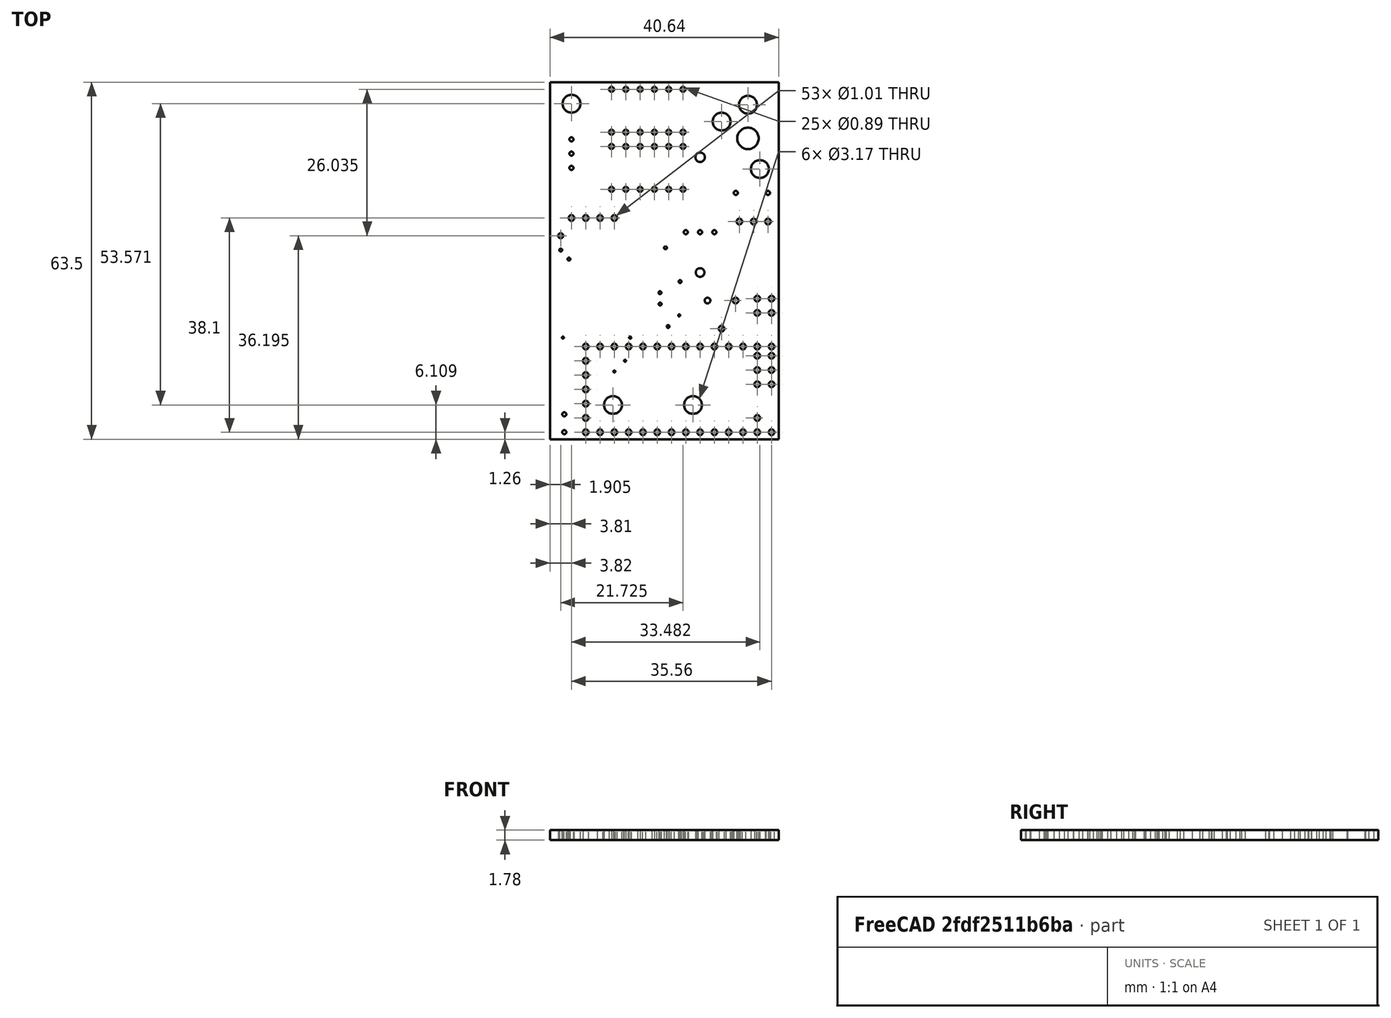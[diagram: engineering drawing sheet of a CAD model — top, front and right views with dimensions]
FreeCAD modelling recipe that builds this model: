
FCSTD DOCUMENT  (FreeCAD 1.0R39109 (Git))
Label: PCB-generated
License: All rights reserved
LicenseURL: https://en.wikipedia.org/wiki/All_rights_reserved
objects: Sketcher::SketchObject×2, PartDesign::Pad×1, PartDesign::Pocket×1, PartDesign::Body×1
note: 11 computed .brp shape members not serialized (recipe doc carries the construction recipe); baked Part::Feature solids carry a one-line shape summary decoded from their .brp

FEATURE [Sketcher::SketchObject] HoleSketch
  ArcFitTolerance = 1e-06
  AttachmentSupport = -> [XY_Plane]
  FullyConstrained = false
  MakeInternals = false
  MapMode = 5
  sketch-geometry (110):
    g0: Circle CenterX=35.1848 CenterY=59.5072 CenterZ=0 NormalX=0 NormalY=0 NormalZ=1 AngleXU=0 Radius=1.5875
    g1: Circle CenterX=35.1752 CenterY=53.5132 CenterZ=0 NormalX=0 NormalY=0 NormalZ=1 AngleXU=0 Radius=1.905
    g2: Circle CenterX=30.4896 CenterY=56.5054 CenterZ=0 NormalX=0 NormalY=0 NormalZ=1 AngleXU=0 Radius=1.5875
    g3: Circle CenterX=3.36742 CenterY=32.0386 CenterZ=0 NormalX=0 NormalY=0 NormalZ=1 AngleXU=0 Radius=0.250152
    g4: Circle CenterX=20.9935 CenterY=20.0698 CenterZ=0 NormalX=0 NormalY=0 NormalZ=1 AngleXU=0 Radius=0.250152
    g5: Circle CenterX=1.905 CenterY=33.6646 CenterZ=0 NormalX=0 NormalY=0 NormalZ=1 AngleXU=0 Radius=0.254962
    g6: Circle CenterX=20.522 CenterY=34.0591 CenterZ=0 NormalX=0 NormalY=0 NormalZ=1 AngleXU=0 Radius=0.254962
    g7: Circle CenterX=19.5407 CenterY=26.0735 CenterZ=0 NormalX=0 NormalY=0 NormalZ=1 AngleXU=0 Radius=0.254962
    g8: Circle CenterX=19.5695 CenterY=24.0627 CenterZ=0 NormalX=0 NormalY=0 NormalZ=1 AngleXU=0 Radius=0.254962
    g9: Circle CenterX=23.6297 CenterY=62.23 CenterZ=0 NormalX=0 NormalY=0 NormalZ=1 AngleXU=0 Radius=0.442576
    g10: Circle CenterX=23.6297 CenterY=54.61 CenterZ=0 NormalX=0 NormalY=0 NormalZ=1 AngleXU=0 Radius=0.442576
    g11: Circle CenterX=21.0897 CenterY=62.23 CenterZ=0 NormalX=0 NormalY=0 NormalZ=1 AngleXU=0 Radius=0.442576
    g12: Circle CenterX=21.0897 CenterY=54.61 CenterZ=0 NormalX=0 NormalY=0 NormalZ=1 AngleXU=0 Radius=0.442576
    g13: Circle CenterX=18.5497 CenterY=62.23 CenterZ=0 NormalX=0 NormalY=0 NormalZ=1 AngleXU=0 Radius=0.442576
    g14: Circle CenterX=18.5497 CenterY=54.61 CenterZ=0 NormalX=0 NormalY=0 NormalZ=1 AngleXU=0 Radius=0.442576
    g15: Circle CenterX=16.0097 CenterY=62.23 CenterZ=0 NormalX=0 NormalY=0 NormalZ=1 AngleXU=0 Radius=0.442576
    g16: Circle CenterX=16.0097 CenterY=54.61 CenterZ=0 NormalX=0 NormalY=0 NormalZ=1 AngleXU=0 Radius=0.442576
    g17: Circle CenterX=13.4697 CenterY=62.23 CenterZ=0 NormalX=0 NormalY=0 NormalZ=1 AngleXU=0 Radius=0.442576
    g18: Circle CenterX=10.9297 CenterY=62.23 CenterZ=0 NormalX=0 NormalY=0 NormalZ=1 AngleXU=0 Radius=0.442576
    g19: Circle CenterX=13.4697 CenterY=54.61 CenterZ=0 NormalX=0 NormalY=0 NormalZ=1 AngleXU=0 Radius=0.442576
    g20: Circle CenterX=10.9297 CenterY=54.61 CenterZ=0 NormalX=0 NormalY=0 NormalZ=1 AngleXU=0 Radius=0.442576
    g21: Circle CenterX=6.35 CenterY=1.26038 CenterZ=0 NormalX=0 NormalY=0 NormalZ=1 AngleXU=0 Radius=0.505114
    g22: Circle CenterX=8.89 CenterY=1.26038 CenterZ=0 NormalX=0 NormalY=0 NormalZ=1 AngleXU=0 Radius=0.505114
    g23: Circle CenterX=11.43 CenterY=1.26038 CenterZ=0 NormalX=0 NormalY=0 NormalZ=1 AngleXU=0 Radius=0.505114
    g24: Circle CenterX=6.35 CenterY=16.5004 CenterZ=0 NormalX=0 NormalY=0 NormalZ=1 AngleXU=0 Radius=0.505114
    g25: Circle CenterX=6.35 CenterY=3.80038 CenterZ=0 NormalX=0 NormalY=0 NormalZ=1 AngleXU=0 Radius=0.505114
    g26: Circle CenterX=6.35 CenterY=6.34038 CenterZ=0 NormalX=0 NormalY=0 NormalZ=1 AngleXU=0 Radius=0.505114
    g27: Circle CenterX=6.35 CenterY=8.88038 CenterZ=0 NormalX=0 NormalY=0 NormalZ=1 AngleXU=0 Radius=0.505114
    g28: Circle CenterX=6.35 CenterY=11.4204 CenterZ=0 NormalX=0 NormalY=0 NormalZ=1 AngleXU=0 Radius=0.505114
    g29: Circle CenterX=6.35 CenterY=13.9604 CenterZ=0 NormalX=0 NormalY=0 NormalZ=1 AngleXU=0 Radius=0.505114
    g30: Circle CenterX=13.97 CenterY=1.26038 CenterZ=0 NormalX=0 NormalY=0 NormalZ=1 AngleXU=0 Radius=0.505114
    g31: Circle CenterX=16.51 CenterY=1.26038 CenterZ=0 NormalX=0 NormalY=0 NormalZ=1 AngleXU=0 Radius=0.505114
    g32: Circle CenterX=19.05 CenterY=1.26038 CenterZ=0 NormalX=0 NormalY=0 NormalZ=1 AngleXU=0 Radius=0.505114
    g33: Circle CenterX=21.59 CenterY=1.26038 CenterZ=0 NormalX=0 NormalY=0 NormalZ=1 AngleXU=0 Radius=0.505114
    g34: Circle CenterX=24.13 CenterY=1.26038 CenterZ=0 NormalX=0 NormalY=0 NormalZ=1 AngleXU=0 Radius=0.505114
    g35: Circle CenterX=26.67 CenterY=1.26038 CenterZ=0 NormalX=0 NormalY=0 NormalZ=1 AngleXU=0 Radius=0.505114
    g36: Circle CenterX=29.21 CenterY=1.26038 CenterZ=0 NormalX=0 NormalY=0 NormalZ=1 AngleXU=0 Radius=0.505114
    g37: Circle CenterX=31.75 CenterY=1.26038 CenterZ=0 NormalX=0 NormalY=0 NormalZ=1 AngleXU=0 Radius=0.505114
    g38: Circle CenterX=34.29 CenterY=1.26038 CenterZ=0 NormalX=0 NormalY=0 NormalZ=1 AngleXU=0 Radius=0.505114
    g39: Circle CenterX=36.83 CenterY=1.26038 CenterZ=0 NormalX=0 NormalY=0 NormalZ=1 AngleXU=0 Radius=0.505114
    g40: Circle CenterX=39.37 CenterY=1.26038 CenterZ=0 NormalX=0 NormalY=0 NormalZ=1 AngleXU=0 Radius=0.505114
    g41: Circle CenterX=8.89 CenterY=16.5004 CenterZ=0 NormalX=0 NormalY=0 NormalZ=1 AngleXU=0 Radius=0.505114
    g42: Circle CenterX=11.43 CenterY=16.5004 CenterZ=0 NormalX=0 NormalY=0 NormalZ=1 AngleXU=0 Radius=0.505114
    g43: Circle CenterX=13.97 CenterY=16.5004 CenterZ=0 NormalX=0 NormalY=0 NormalZ=1 AngleXU=0 Radius=0.505114
    g44: Circle CenterX=16.51 CenterY=16.5004 CenterZ=0 NormalX=0 NormalY=0 NormalZ=1 AngleXU=0 Radius=0.505114
    g45: Circle CenterX=19.05 CenterY=16.5004 CenterZ=0 NormalX=0 NormalY=0 NormalZ=1 AngleXU=0 Radius=0.505114
    g46: Circle CenterX=21.59 CenterY=16.5004 CenterZ=0 NormalX=0 NormalY=0 NormalZ=1 AngleXU=0 Radius=0.505114
    g47: Circle CenterX=24.13 CenterY=16.5004 CenterZ=0 NormalX=0 NormalY=0 NormalZ=1 AngleXU=0 Radius=0.505114
    g48: Circle CenterX=26.67 CenterY=16.5004 CenterZ=0 NormalX=0 NormalY=0 NormalZ=1 AngleXU=0 Radius=0.505114
    g49: Circle CenterX=29.21 CenterY=16.5004 CenterZ=0 NormalX=0 NormalY=0 NormalZ=1 AngleXU=0 Radius=0.505114
    g50: Circle CenterX=31.75 CenterY=16.5004 CenterZ=0 NormalX=0 NormalY=0 NormalZ=1 AngleXU=0 Radius=0.505114
    g51: Circle CenterX=34.29 CenterY=16.5004 CenterZ=0 NormalX=0 NormalY=0 NormalZ=1 AngleXU=0 Radius=0.505114
    g52: Circle CenterX=36.83 CenterY=16.5004 CenterZ=0 NormalX=0 NormalY=0 NormalZ=1 AngleXU=0 Radius=0.505114
    g53: Circle CenterX=39.37 CenterY=16.5004 CenterZ=0 NormalX=0 NormalY=0 NormalZ=1 AngleXU=0 Radius=0.505114
    g54: Circle CenterX=36.83 CenterY=3.80038 CenterZ=0 NormalX=0 NormalY=0 NormalZ=1 AngleXU=0 Radius=0.505114
    g55: Circle CenterX=25.4096 CenterY=6.10947 CenterZ=0 NormalX=0 NormalY=0 NormalZ=1 AngleXU=0 Radius=1.5875
    g56: Circle CenterX=3.81962 CenterY=59.6804 CenterZ=0 NormalX=0 NormalY=0 NormalZ=1 AngleXU=0 Radius=1.5875
    g57: Circle CenterX=11.1895 CenterY=6.10947 CenterZ=0 NormalX=0 NormalY=0 NormalZ=1 AngleXU=0 Radius=1.5875
    g58: Circle CenterX=26.67 CenterY=29.6622 CenterZ=0 NormalX=0 NormalY=0 NormalZ=1 AngleXU=0 Radius=0.774508
    g59: Circle CenterX=26.67 CenterY=50.165 CenterZ=0 NormalX=0 NormalY=0 NormalZ=1 AngleXU=0 Radius=0.846667
    g60: Circle CenterX=39.37 CenterY=12.3248 CenterZ=0 NormalX=0 NormalY=0 NormalZ=1 AngleXU=0 Radius=0.505114
    g61: Circle CenterX=39.37 CenterY=9.78477 CenterZ=0 NormalX=0 NormalY=0 NormalZ=1 AngleXU=0 Radius=0.505114
    g62: Circle CenterX=36.83 CenterY=9.78477 CenterZ=0 NormalX=0 NormalY=0 NormalZ=1 AngleXU=0 Radius=0.505114
    g63: Circle CenterX=39.37 CenterY=14.8648 CenterZ=0 NormalX=0 NormalY=0 NormalZ=1 AngleXU=0 Radius=0.505114
    g64: Circle CenterX=36.83 CenterY=12.3248 CenterZ=0 NormalX=0 NormalY=0 NormalZ=1 AngleXU=0 Radius=0.505114
    g65: Circle CenterX=36.83 CenterY=14.8648 CenterZ=0 NormalX=0 NormalY=0 NormalZ=1 AngleXU=0 Radius=0.505114
    g66: Circle CenterX=30.48 CenterY=19.6754 CenterZ=0 NormalX=0 NormalY=0 NormalZ=1 AngleXU=0 Radius=0.505114
    g67: Circle CenterX=32.9815 CenterY=24.6784 CenterZ=0 NormalX=0 NormalY=0 NormalZ=1 AngleXU=0 Radius=0.505114
    g68: Circle CenterX=27.9881 CenterY=24.6784 CenterZ=0 NormalX=0 NormalY=0 NormalZ=1 AngleXU=0 Radius=0.509924
    g69: Circle CenterX=39.37 CenterY=22.4848 CenterZ=0 NormalX=0 NormalY=0 NormalZ=1 AngleXU=0 Radius=0.505114
    g70: Circle CenterX=36.83 CenterY=22.4848 CenterZ=0 NormalX=0 NormalY=0 NormalZ=1 AngleXU=0 Radius=0.505114
    g71: Circle CenterX=39.37 CenterY=25.0248 CenterZ=0 NormalX=0 NormalY=0 NormalZ=1 AngleXU=0 Radius=0.505114
    g72: Circle CenterX=36.83 CenterY=25.0248 CenterZ=0 NormalX=0 NormalY=0 NormalZ=1 AngleXU=0 Radius=0.505114
    g73: Circle CenterX=38.735 CenterY=38.7254 CenterZ=0 NormalX=0 NormalY=0 NormalZ=1 AngleXU=0 Radius=0.505114
    g74: Circle CenterX=33.655 CenterY=38.7254 CenterZ=0 NormalX=0 NormalY=0 NormalZ=1 AngleXU=0 Radius=0.505114
    g75: Circle CenterX=36.195 CenterY=38.7254 CenterZ=0 NormalX=0 NormalY=0 NormalZ=1 AngleXU=0 Radius=0.505114
    g76: Circle CenterX=37.3014 CenterY=48.058 CenterZ=0 NormalX=0 NormalY=0 NormalZ=1 AngleXU=0 Radius=1.5875
    g77: Circle CenterX=3.81 CenterY=48.26 CenterZ=0 NormalX=0 NormalY=0 NormalZ=1 AngleXU=0 Radius=0.365606
    g78: Circle CenterX=3.81 CenterY=53.34 CenterZ=0 NormalX=0 NormalY=0 NormalZ=1 AngleXU=0 Radius=0.365606
    g79: Circle CenterX=3.81 CenterY=50.8 CenterZ=0 NormalX=0 NormalY=0 NormalZ=1 AngleXU=0 Radius=0.365606
    g80: Circle CenterX=29.21 CenterY=36.83 CenterZ=0 NormalX=0 NormalY=0 NormalZ=1 AngleXU=0 Radius=0.365606
    g81: Circle CenterX=24.13 CenterY=36.83 CenterZ=0 NormalX=0 NormalY=0 NormalZ=1 AngleXU=0 Radius=0.365606
    g82: Circle CenterX=26.67 CenterY=36.83 CenterZ=0 NormalX=0 NormalY=0 NormalZ=1 AngleXU=0 Radius=0.365606
    g83: Circle CenterX=3.81 CenterY=39.3604 CenterZ=0 NormalX=0 NormalY=0 NormalZ=1 AngleXU=0 Radius=0.505114
    g84: Circle CenterX=6.35 CenterY=39.3604 CenterZ=0 NormalX=0 NormalY=0 NormalZ=1 AngleXU=0 Radius=0.505114
    g85: Circle CenterX=8.89 CenterY=39.3604 CenterZ=0 NormalX=0 NormalY=0 NormalZ=1 AngleXU=0 Radius=0.505114
    g86: Circle CenterX=11.43 CenterY=39.3604 CenterZ=0 NormalX=0 NormalY=0 NormalZ=1 AngleXU=0 Radius=0.505114
    g87: Circle CenterX=23.1102 CenterY=28.0458 CenterZ=0 NormalX=0 NormalY=0 NormalZ=1 AngleXU=0 Radius=0.254962
    g88: Circle CenterX=1.905 CenterY=36.195 CenterZ=0 NormalX=0 NormalY=0 NormalZ=1 AngleXU=0 Radius=0.442576
    g89: Circle CenterX=23.6297 CenterY=52.07 CenterZ=0 NormalX=0 NormalY=0 NormalZ=1 AngleXU=0 Radius=0.442576
    g90: Circle CenterX=23.6297 CenterY=44.45 CenterZ=0 NormalX=0 NormalY=0 NormalZ=1 AngleXU=0 Radius=0.442576
    g91: Circle CenterX=21.0897 CenterY=52.07 CenterZ=0 NormalX=0 NormalY=0 NormalZ=1 AngleXU=0 Radius=0.442576
    g92: Circle CenterX=21.0897 CenterY=44.45 CenterZ=0 NormalX=0 NormalY=0 NormalZ=1 AngleXU=0 Radius=0.442576
    g93: Circle CenterX=18.5497 CenterY=52.07 CenterZ=0 NormalX=0 NormalY=0 NormalZ=1 AngleXU=0 Radius=0.442576
    g94: Circle CenterX=18.5497 CenterY=44.45 CenterZ=0 NormalX=0 NormalY=0 NormalZ=1 AngleXU=0 Radius=0.442576
    g95: Circle CenterX=16.0097 CenterY=52.07 CenterZ=0 NormalX=0 NormalY=0 NormalZ=1 AngleXU=0 Radius=0.442576
    g96: Circle CenterX=16.0097 CenterY=44.45 CenterZ=0 NormalX=0 NormalY=0 NormalZ=1 AngleXU=0 Radius=0.442576
    g97: Circle CenterX=13.4697 CenterY=52.07 CenterZ=0 NormalX=0 NormalY=0 NormalZ=1 AngleXU=0 Radius=0.442576
    g98: Circle CenterX=10.9297 CenterY=52.07 CenterZ=0 NormalX=0 NormalY=0 NormalZ=1 AngleXU=0 Radius=0.442576
    g99: Circle CenterX=13.4697 CenterY=44.45 CenterZ=0 NormalX=0 NormalY=0 NormalZ=1 AngleXU=0 Radius=0.442576
    g100: Circle CenterX=10.9297 CenterY=44.45 CenterZ=0 NormalX=0 NormalY=0 NormalZ=1 AngleXU=0 Radius=0.442576
    g101: Circle CenterX=14.249 CenterY=18.0783 CenterZ=0 NormalX=0 NormalY=0 NormalZ=1 AngleXU=0 Radius=0.182803
    g102: Circle CenterX=2.28985 CenterY=18.0783 CenterZ=0 NormalX=0 NormalY=0 NormalZ=1 AngleXU=0 Radius=0.177992
    g103: Circle CenterX=22.9562 CenterY=22.0326 CenterZ=0 NormalX=0 NormalY=0 NormalZ=1 AngleXU=0 Radius=0.173182
    g104: Circle CenterX=13.335 CenterY=13.97 CenterZ=0 NormalX=0 NormalY=0 NormalZ=1 AngleXU=0 Radius=0.173182
    g105: Circle CenterX=11.43 CenterY=12.065 CenterZ=0 NormalX=0 NormalY=0 NormalZ=1 AngleXU=0 Radius=0.173182
    g106: Circle CenterX=38.735 CenterY=43.815 CenterZ=0 NormalX=0 NormalY=0 NormalZ=1 AngleXU=0 Radius=0.365606
    g107: Circle CenterX=33.02 CenterY=43.815 CenterZ=0 NormalX=0 NormalY=0 NormalZ=1 AngleXU=0 Radius=0.365606
    g108: Circle CenterX=2.54 CenterY=1.27 CenterZ=0 NormalX=0 NormalY=0 NormalZ=1 AngleXU=0 Radius=0.365606
    g109: Circle CenterX=2.54 CenterY=4.445 CenterZ=0 NormalX=0 NormalY=0 NormalZ=1 AngleXU=0 Radius=0.365606
FEATURE [Sketcher::SketchObject] MainSketch
  ArcFitTolerance = 1e-06
  AttachmentSupport = -> [XY_Plane]
  FullyConstrained = false
  MakeInternals = false
  MapMode = 5
  sketch-geometry (4):
    g0: LineSegment StartX=0 StartY=0 StartZ=0 EndX=40.64 EndY=0 EndZ=0
    g1: LineSegment StartX=40.64 StartY=0 StartZ=0 EndX=40.64 EndY=63.5 EndZ=0
    g2: LineSegment StartX=40.64 StartY=63.5 StartZ=0 EndX=0 EndY=63.5 EndZ=0
    g3: LineSegment StartX=0 StartY=63.5 StartZ=0 EndX=0 EndY=0 EndZ=0
  constraints (4):
    c: Horizontal(g0)
    c: Horizontal(g2)
    c: Vertical(g1)
    c: Vertical(g3)
FEATURE [PartDesign::Pad] Main
  Direction = (0,0,1)
  Length = 1.778
  Length2 = 100.076
  Profile = -> MainSketch
  Refine = true
  Suppressed = false
  Type = 0
FEATURE [PartDesign::Pocket] Holes
  BaseFeature = -> Main
  Direction = (0,0,-1)
  Length = 3.556
  Length2 = 5
  Profile = -> HoleSketch
  Refine = true
  Reversed = true
  Suppressed = false
  Type = 0
FEATURE [PartDesign::Body] Body
  AllowCompound = false
  Group = -> [MainSketch,Main,HoleSketch,Holes]
  Origin = -> Origin
  Tip = -> Holes
